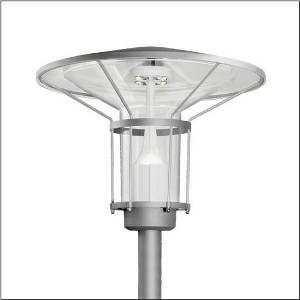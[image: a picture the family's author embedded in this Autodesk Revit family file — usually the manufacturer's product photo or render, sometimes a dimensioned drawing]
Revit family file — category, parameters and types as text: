
# Revit family: laterne_classic_iq___pl1_2s_5xa5245of14h_0553
name_source: partatom
category: Lighting Fixtures
units: mm (PartAtom-declared; Revit-internal decimal feet)

## family parameters
Cut with Voids When Loaded = No
Host = Face
Light Source = No
Part Type = Normal
Room Calculation Point = No
Round Connector Dimension = Use Diameter
Shared = No

## types (1)
- --- (1 x LED, 2670 lm, 21.8 W, 2700K)
    Apparent Load = 22 VA
    CIE Flux Codes = 21 60 93 97 100
    Color Rendering = 70
    Color Temperature = 2700K
    Default Elevation = 1800 mm
    Description = Lantern Classic iQ, mast luminaire, Module 540 iQ-SR, primary light control with 3 zone facetted reflector, of plastic, silver coated, highly specular, structured, primary optical cover: cover, of PMMA, transparent, light distribution: PL1.2s, light emission: direct distribution, primary light characteristic: symmetric, installation type: post-top, LED, High Power LED, rated luminous flux: 2.970lm, luminous efficacy: 136lm/W, light colour: 727, colour temperature: 2700K, control gear: iQ Street-Remote, control: pre-setting: logarithmic dimming characteristic, Street-Remote, Auto-Match, Temp-Guard, Lumen-Switch, Night-Set, Smart-Wire, Light-Fading, Desk-Remote (wireless, voltage-free reading and setting of iQ features in the workshop via application-optimized NFC function/RFID function), optimised constant luminous flux control (CLO 2.0), with terminal, 6-pole, max. 2.5mm², mains connection: 230..240V, AC, 50/60Hz, start of lifetime: 22W, end of service life: 23W, reduction: 11W, luminaire housing, upper part, of glass-fibre reinforced polyester, coated, Siteco® metallic grey (DB 702S), diameter: 750mm, height: 596mm, spigot size: d x l = 76 x 70mm (post-top) | with reducer (optional accessory) 60 x 70mm, mounting height: 3..5m, post-top mast mounting element, of diecast aluminium, coated, Siteco® metallic grey (DB 702S), Module 540 iQ-SR, traffic white (RAL 9016), equipment: standard, protection rating (complete): IP65, insulation class (complete): insulation class II (safety insulation), certification: CE, ENEC, VDE, packaging unit: 1 piece

Light Distribution: PL1.2s
    Height = 596 mm
    Lamp = 1 x LED
    Lamp Light Flux = 2670 lm
    Lamp Power = 21.8 W
    Lamp count = 1
    Length = 750 mm
    Luminous efficacy = 122 lm/W
    Manufacturer = Siteco
    ModVariant = No
    Model = 5XA5245OF14H
    Number of Poles = 1
    OnlyDefault = Yes
    Power Factor = 1
    Product Name = Laterne Classic iQ | PL1.2s
    Product group = mast luminaire | pylon top
    ProductGroupID = 6100
    Protection Class = Protection class II
    Protection Degree = IP 65
    RLX_Detail_Level = 1
    RLX_Emergency_Light_Flux = 0 lm
    RLX_Emergency_Type = 0
    RLX_Emergency_Type_DB = No
    RlxData = <blob elided: 37781 chars, md5=76ba73d9>
    Socket = socket
    Standby Power = 0 W
    System Light Flux = 2670 lm
    System Power = 22 W
    Type Comments = factory setting: luminous flux: 100 % | dim-lin: 254 | 456 mA
    Type Image = l_1006052.jpg
    URL = http://relux.com
    VarID = @adj_145632
    Voltage = 0 V
    Weight = 0.00 kg
    Width = 0 mm  [stored 0 ft]

note: [stored X ft] marks values corroborated as IEEE doubles in the binary element streams (Revit-internal decimal feet)

## geometry (parser evidence)
native form markers: Blend x4, Sweep x10
no freeform markers — native parametric forms only
